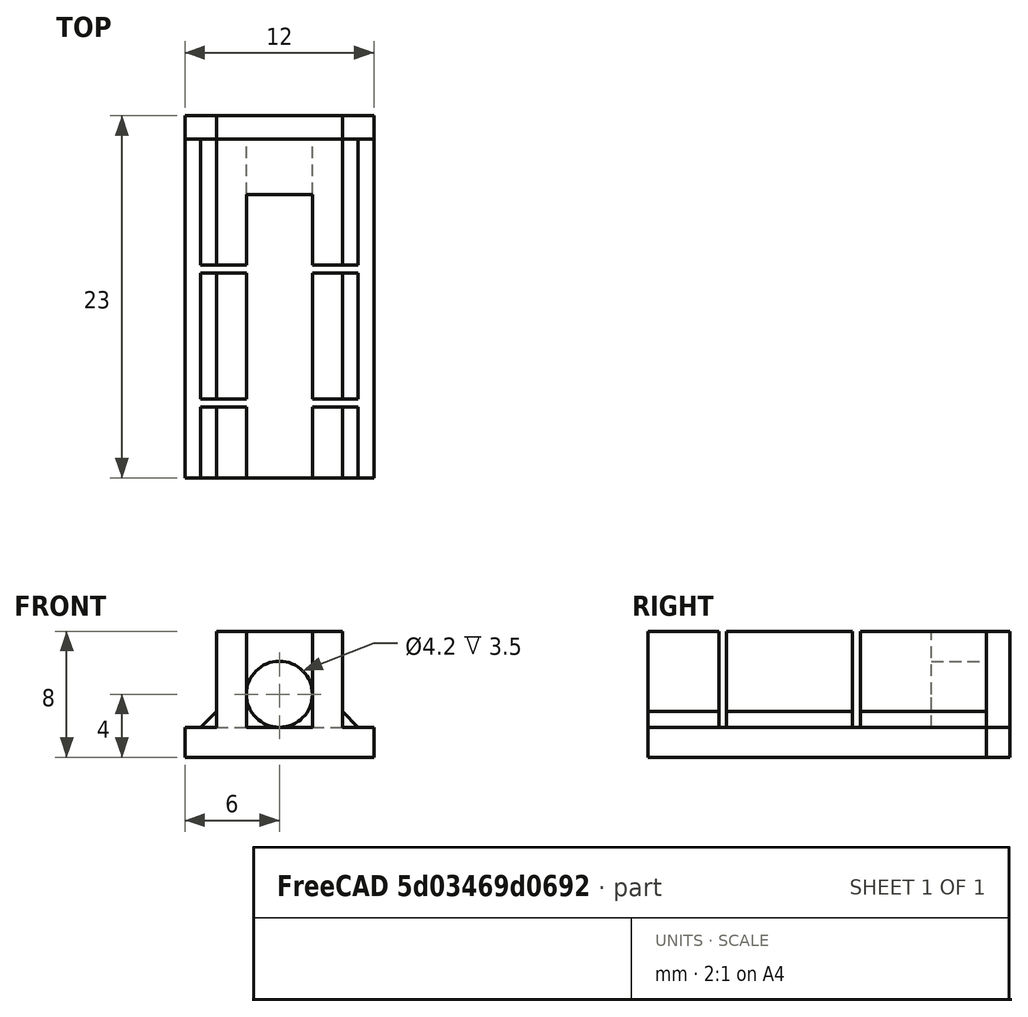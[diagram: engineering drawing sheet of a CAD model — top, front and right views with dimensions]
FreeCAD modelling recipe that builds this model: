
FCSTD DOCUMENT  (FreeCAD 0.18R16146 (Git))
Label: mosquito-ptfe-cutter
License: All rights reserved
LicenseURL: http://en.wikipedia.org/wiki/All_rights_reserved
objects: Part::Box×8, Part::Cut×4, Part::Cylinder×2, Part::MultiFuse×1, Part::Feature×1, Part::Chamfer×1
note: 17 computed .brp shape members not serialized (recipe doc carries the construction recipe); baked Part::Feature solids carry a one-line shape summary decoded from their .brp

FEATURE [Part::Box] Box  label="Cube"
  AttacherType = Attacher::AttachEngine3D
  Height = 8
  Length = 8
  Placement = pos=(-4,13,0) rot=(0,0,1;0rad)
  Width = 5
FEATURE [Part::Cylinder] Cylinder
  Angle = 360
  AttacherType = Attacher::AttachEngine3D
  Height = 25
  Placement = pos=(0,-8.5,4) rot=(1,0,0;4.71239rad)
  Radius = 2.1
FEATURE [Part::Cut] Cut
  Base = -> Box
  Tool = -> Cylinder
FEATURE [Part::Box] Box001  label="Cube001"
  AttacherType = Attacher::AttachEngine3D
  Height = 8
  Length = 1.9
  Placement = pos=(-4,0,0) rot=(0,0,1;0rad)
  Width = 13
FEATURE [Part::Box] Box002  label="Cube002"
  AttacherType = Attacher::AttachEngine3D
  Height = 8
  Length = 1.9
  Placement = pos=(2.1,0,0) rot=(0,0,1;0rad)
  Width = 13
FEATURE [Part::Box] Box003  label="Cube003"
  AttacherType = Attacher::AttachEngine3D
  Height = 8
  Length = 1.9
  Placement = pos=(-4,-5,0) rot=(0,0,1;0rad)
  Width = 4.5
FEATURE [Part::Box] Box004  label="Cube004"
  AttacherType = Attacher::AttachEngine3D
  Height = 8
  Length = 1.9
  Placement = pos=(2.1,-5,0) rot=(0,0,1;0rad)
  Width = 4.5
FEATURE [Part::Box] Box005  label="Cube005"
  AttacherType = Attacher::AttachEngine3D
  Height = 1.9
  Length = 12
  Placement = pos=(-6,-5,0) rot=(0,0,1;0rad)
  Width = 23
FEATURE [Part::MultiFuse] Fusion
  Shapes = -> [Box001,Box002,Box004,Cut,Box003,Box005]
FEATURE [Part::Box] Box006  label="Cube006"
  AttacherType = Attacher::AttachEngine3D
  Height = 10
  Length = 10
  Placement = pos=(-5,8,1.9) rot=(0,0,1;0rad)
  Width = 0.5
FEATURE [Part::Cut] Cut001
  Base = -> Fusion
  Tool = -> Box006
FEATURE [Part::Feature] Cut001001  label="Cut002"
  shape: bbox 12 x 23 x 8 mm, 36 faces (baked)
FEATURE [Part::Chamfer] Chamfer
  Base = -> Cut001001
  Edges = 6 edges r=1: [Edge33,Edge46,Edge47,Edge54,Edge55,Edge61]
FEATURE [Part::Cylinder] Cylinder001
  Angle = 360
  AttacherType = Attacher::AttachEngine3D
  Height = 10
  Placement = pos=(0,11,4) rot=(1,0,0;4.71239rad)
  Radius = 1.5
FEATURE [Part::Cut] Cut001002
  Base = -> Chamfer
  Tool = -> Cylinder001
FEATURE [Part::Box] Box007  label="Cube007"
  AttacherType = Attacher::AttachEngine3D
  Height = 10
  Length = 12
  Placement = pos=(-6,16.5,0) rot=(0,0,1;0rad)
  Width = 10
FEATURE [Part::Cut] Cut001003
  Base = -> Cut001002
  Tool = -> Box007
